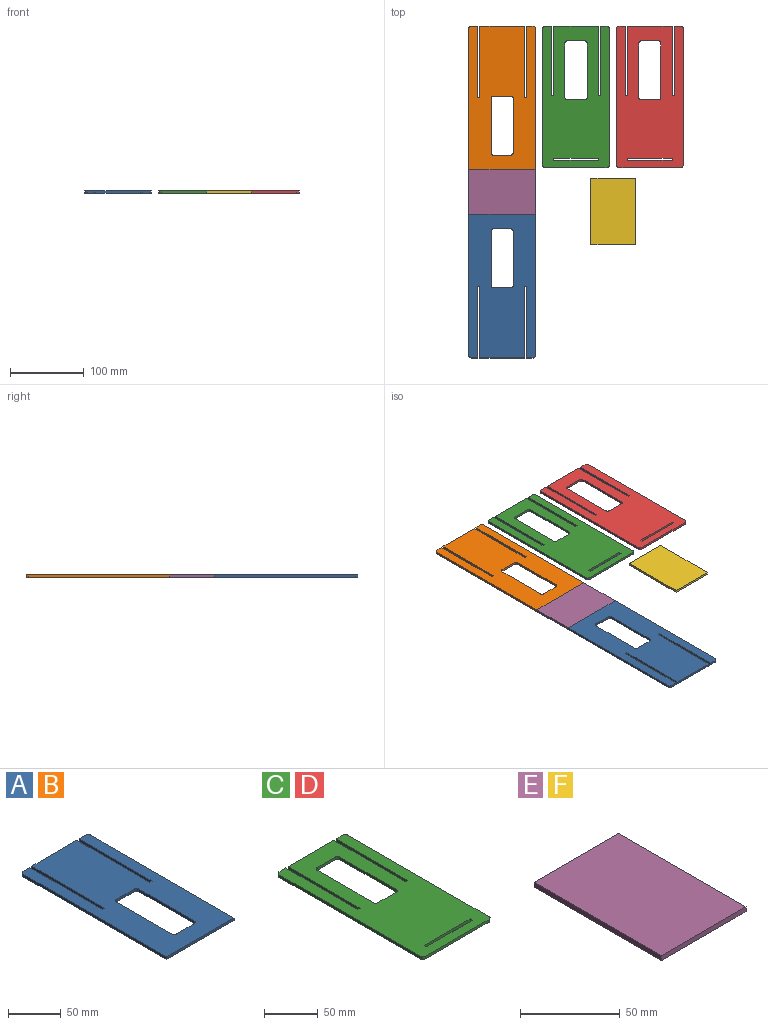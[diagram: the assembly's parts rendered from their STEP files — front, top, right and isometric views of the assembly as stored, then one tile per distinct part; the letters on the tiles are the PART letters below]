
ASSEMBLY  parts=6 mates=9
PART A: 24 faces, bbox 90x195x3 mm
  f0: plane 74x3mm, normal (1,0,0), area 222mm2, adj f16,f17,f20,f23
  f1: plane 24x3mm, normal (0,-1,0), area 72mm2, adj f16,f17,f20,f21
  f2: plane 74x3mm, normal (-1,0,0), area 222mm2, adj f16,f17,f21,f22
  f3: plane 3x3mm, normal (0,1,0), area 9mm2, adj f4,f14,f16,f17
  f4: plane 97.5x3mm, normal (1,0,0), area 292.5mm2, adj f3,f5,f16,f17
  f5: plane 9x3mm, normal (0,1,0), area 27mm2, adj f4,f16,f17,f18
  f6: plane 192x3mm, normal (-1,0,0), area 576mm2, adj f7,f16,f17,f18
  f7: plane 90x3mm, normal (0,-1,0), area 270mm2, adj f6,f8,f16,f17
  f8: plane 192x3mm, normal (1,0,0), area 576mm2, adj f7,f16,f17,f19
  f9: plane 9x3mm, normal (0,1,0), area 27mm2, adj f10,f16,f17,f19
  f10: plane 97.5x3mm, normal (-1,0,0), area 292.5mm2, adj f9,f11,f16,f17
  f11: plane 3x3mm, normal (0,1,0), area 9mm2, adj f10,f12,f16,f17
  f12: plane 97.5x3mm, normal (1,0,0), area 292.5mm2, adj f11,f13,f16,f17
  f13: plane 60x3mm, normal (0,1,0), area 180mm2, adj f12,f14,f16,f17
  f14: plane 97.5x3mm, normal (-1,0,0), area 292.5mm2, adj f3,f13,f16,f17
  f15: plane 24x3mm, normal (0,1,0), area 72mm2, adj f16,f17,f22,f23
  f16: plane 195x90mm, normal (0,0,1), area 14568.9mm2, adj f0,f1,f2,f3,f4,f5,f6,f7
  f17: plane 195x90mm, normal (0,0,-1), area 14568.9mm2, adj f0,f1,f2,f3,f4,f5,f6,f7
  f18: cylinder r=3mm len=3mm, axis (0,0,-1), area 14.1mm2, adj f5,f6,f16,f17
  f19: cylinder r=3mm len=3mm, axis (0,0,1), area 14.1mm2, adj f8,f9,f16,f17
  f20: cylinder r=3mm len=3mm, axis (0,0,-1), area 14.1mm2, adj f0,f1,f16,f17
  f21: cylinder r=3mm len=3mm, axis (0,0,1), area 14.1mm2, adj f1,f2,f16,f17
  f22: cylinder r=3mm len=3mm, axis (0,0,-1), area 14.1mm2, adj f2,f15,f16,f17
  f23: cylinder r=3mm len=3mm, axis (0,0,1), area 14.1mm2, adj f0,f15,f16,f17
PART B: same geometry as A
PART C: 30 faces, bbox 90x192x3 mm
  f0: plane 3x3mm, normal (1,0,0), area 9mm2, adj f1,f19,f20,f21
  f1: plane 60x3mm, normal (0,-1,0), area 180mm2, adj f0,f2,f20,f21
  f2: plane 3x3mm, normal (-1,0,0), area 9mm2, adj f1,f19,f20,f21
  f3: plane 74x3mm, normal (1,0,0), area 222mm2, adj f20,f21,f26,f29
  f4: plane 24x3mm, normal (0,-1,0), area 72mm2, adj f20,f21,f26,f27
  f5: plane 74x3mm, normal (-1,0,0), area 222mm2, adj f20,f21,f27,f28
  f6: plane 3x3mm, normal (0,1,0), area 9mm2, adj f7,f18,f20,f21
  f7: plane 94.5x3mm, normal (1,0,0), area 283.5mm2, adj f6,f8,f20,f21
  f8: plane 9x3mm, normal (0,1,0), area 27mm2, adj f7,f20,f21,f22
  f9: plane 186x3mm, normal (-1,0,0), area 558mm2, adj f20,f21,f22,f23
  f10: plane 84x3mm, normal (0,-1,0), area 252mm2, adj f20,f21,f23,f24
  f11: plane 186x3mm, normal (1,0,0), area 558mm2, adj f20,f21,f24,f25
  f12: plane 9x3mm, normal (0,1,0), area 27mm2, adj f13,f20,f21,f25
  f13: plane 94.5x3mm, normal (-1,0,0), area 283.5mm2, adj f12,f14,f20,f21
  f14: plane 3x3mm, normal (0,1,0), area 9mm2, adj f13,f15,f20,f21
  f15: plane 94.5x3mm, normal (1,0,0), area 283.5mm2, adj f14,f16,f20,f21
  f16: plane 60x3mm, normal (0,1,0), area 180mm2, adj f15,f18,f20,f21
  f17: plane 24x3mm, normal (0,1,0), area 72mm2, adj f20,f21,f28,f29
  f18: plane 94.5x3mm, normal (-1,0,0), area 283.5mm2, adj f6,f16,f20,f21
  f19: plane 60x3mm, normal (0,1,0), area 180mm2, adj f0,f2,f20,f21
  f20: plane 192x90mm, normal (0,0,1), area 14133mm2, adj f0,f1,f2,f3,f4,f5,f6,f7
  f21: plane 192x90mm, normal (0,0,-1), area 14133mm2, adj f0,f1,f2,f3,f4,f5,f6,f7
  f22: cylinder r=3mm len=3mm, axis (0,0,-1), area 14.1mm2, adj f8,f9,f20,f21
  f23: cylinder r=3mm len=3mm, axis (0,0,1), area 14.1mm2, adj f9,f10,f20,f21
  f24: cylinder r=3mm len=3mm, axis (0,0,-1), area 14.1mm2, adj f10,f11,f20,f21
  f25: cylinder r=3mm len=3mm, axis (0,0,1), area 14.1mm2, adj f11,f12,f20,f21
  f26: cylinder r=3mm len=3mm, axis (0,0,-1), area 14.1mm2, adj f3,f4,f20,f21
  f27: cylinder r=3mm len=3mm, axis (0,0,1), area 14.1mm2, adj f4,f5,f20,f21
  f28: cylinder r=3mm len=3mm, axis (0,0,-1), area 14.1mm2, adj f5,f17,f20,f21
  f29: cylinder r=3mm len=3mm, axis (0,0,1), area 14.1mm2, adj f3,f17,f20,f21
PART D: same geometry as C
PART E: 6 faces, bbox 60x90x3 mm
  f0: plane 90x3mm, normal (-1,0,0), area 270mm2, adj f1,f3,f4,f5
  f1: plane 60x3mm, normal (0,-1,0), area 180mm2, adj f0,f2,f4,f5
  f2: plane 90x3mm, normal (1,0,0), area 270mm2, adj f1,f3,f4,f5
  f3: plane 60x3mm, normal (0,1,0), area 180mm2, adj f0,f2,f4,f5
  f4: plane 90x60mm, normal (0,0,1), area 5400mm2, adj f0,f1,f2,f3
  f5: plane 90x60mm, normal (0,0,-1), area 5400mm2, adj f0,f1,f2,f3
PART F: same geometry as E
PLACE A rot(axis=(0,0,-1),180deg) t=(45,-30,-3)mm
PLACE B rot(axis=(0,0,1),0deg) t=(-45,30,-3)mm
PLACE C rot(axis=(0,0,1),0deg) t=(55.24,33,-3)mm
PLACE D rot(axis=(0,0,1),0deg) t=(155.4,33,-3)mm
PLACE E rot(axis=(0,0,-1),90deg) t=(-45,30,-3)mm
PLACE F rot(axis=(0,0,1),0deg) t=(120.48,-71.43,-3)mm
MATE planar D.f16 <-> C.f16  axis (0,1,0) through (200.4,225,-1.5)mm
MATE fastened B.f7 <-> E.f0  axis (0,-1,0) through (0,30,-1.5)mm
MATE planar E.f4 <-> F.f4  axis (0,0,1) through (0,0,0)mm
MATE planar B.f16 <-> A.f16  axis (0,0,1) through (0,131.67,0)mm
MATE planar D.f20 <-> B.f16  axis (0,0,1) through (200.4,122.03,0)mm
MATE fastened A.f7 <-> E.f2  axis (0,1,0) through (0,-30,-1.5)mm
MATE planar D.f20 <-> C.f20  axis (0,0,1) through (200.4,125,0)mm
MATE planar D.f16 <-> B.f13  axis (0,1,0) through (200.4,225,-1.5)mm
MATE planar B.f16 <-> E.f4  axis (0,0,1) through (0,130,0)mm
